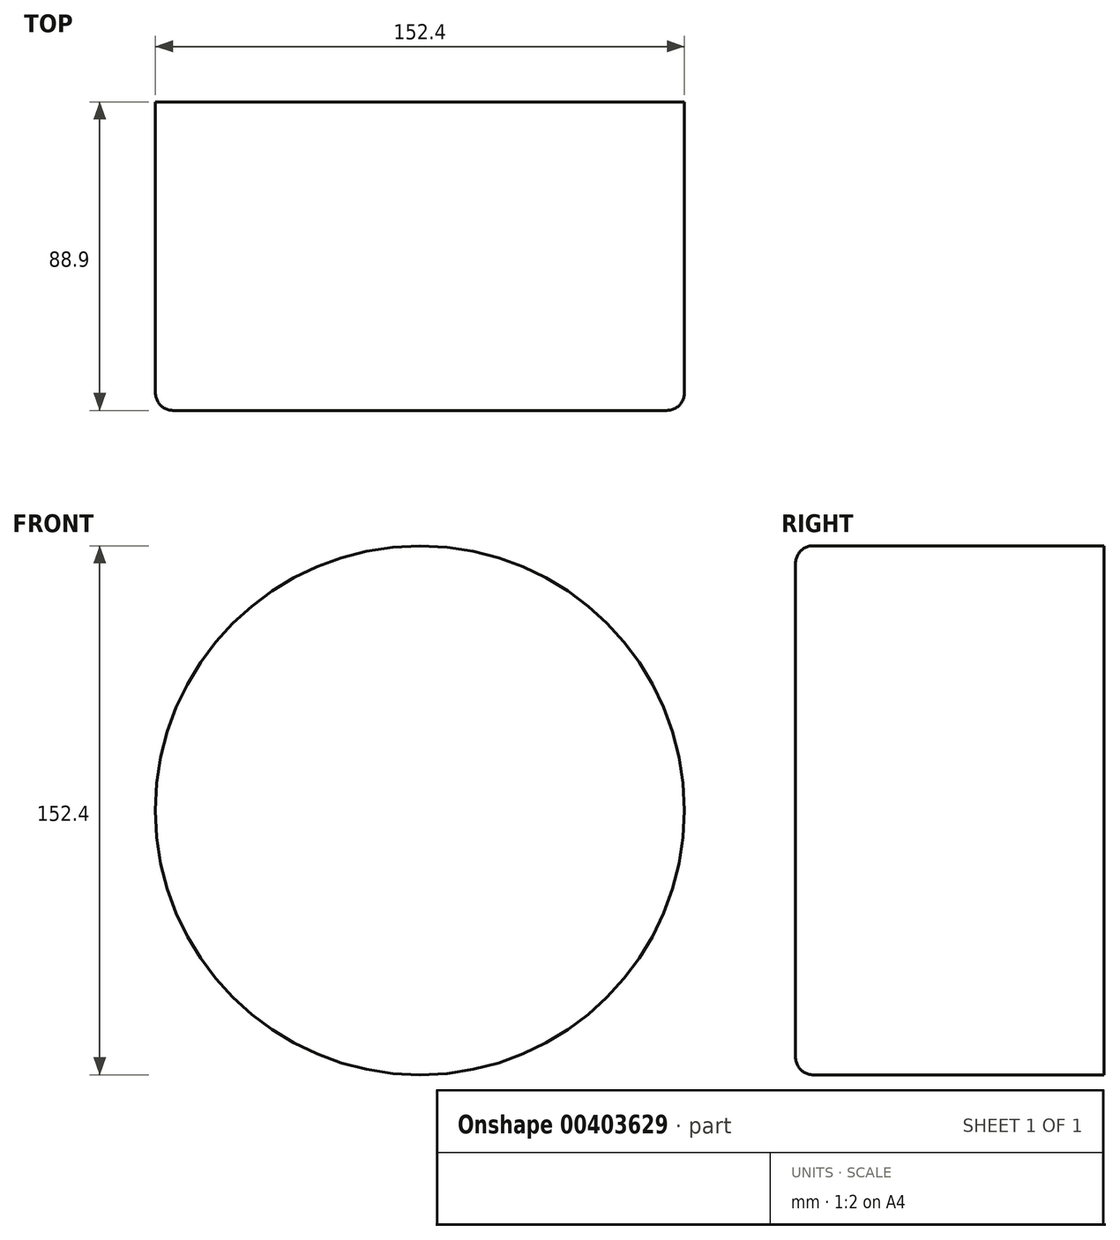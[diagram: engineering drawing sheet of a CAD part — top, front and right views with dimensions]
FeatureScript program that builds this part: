
annotation { "Feature Type Name" : "Feature", "Feature Type Description" : "" }
export const myFeature = defineFeature(function(context is Context, id is Id, definition is map)
    precondition{}
    {
        {
            var Q0;
            Q0=qCreatedBy(makeId("Front.planeOp"),FACE);
            var sketch = newSketch(context, id + "F0", { "sketchPlane" : qUnion([Q0])});
            skCircle(sketch, "E0", {"center": v(0, 0) * mm, "radius": 76.2 * mm});
            skSolve(sketch);
        }
        {
            var Q0;
            Q0=makeQuery(id+"F0.imprint","IMPRINT",FACE,{"disambiguationData":[TD([[makeQuery(id+"F0.imprint","IMPRINT",EDGE,{"derivedFrom":sQuery(id+"F0.wireOp",EDGE,"E0")}),1.0]])]});
            extrude(context, id + "F1", {"entities" : qUnion([Q0]), "endBound" : BoundingType.SYMMETRIC, "depth" : 88.9 * mm});
        }
        {
            var Q0;
            Q0=makeQuery(id+"F1.opExtrude","CAP_EDGE",EDGE,{"disambiguationData":[OSD([sQuery(id+"F0.wireOp",EDGE,"E0")])],"isStart":false});
            fillet(context, id + "F2", {"entities" : qUnion([Q0]), "radius" : 5.08 * mm, "tangentPropagation" : true, "allowEdgeOverflow" : false});
        }
    });
